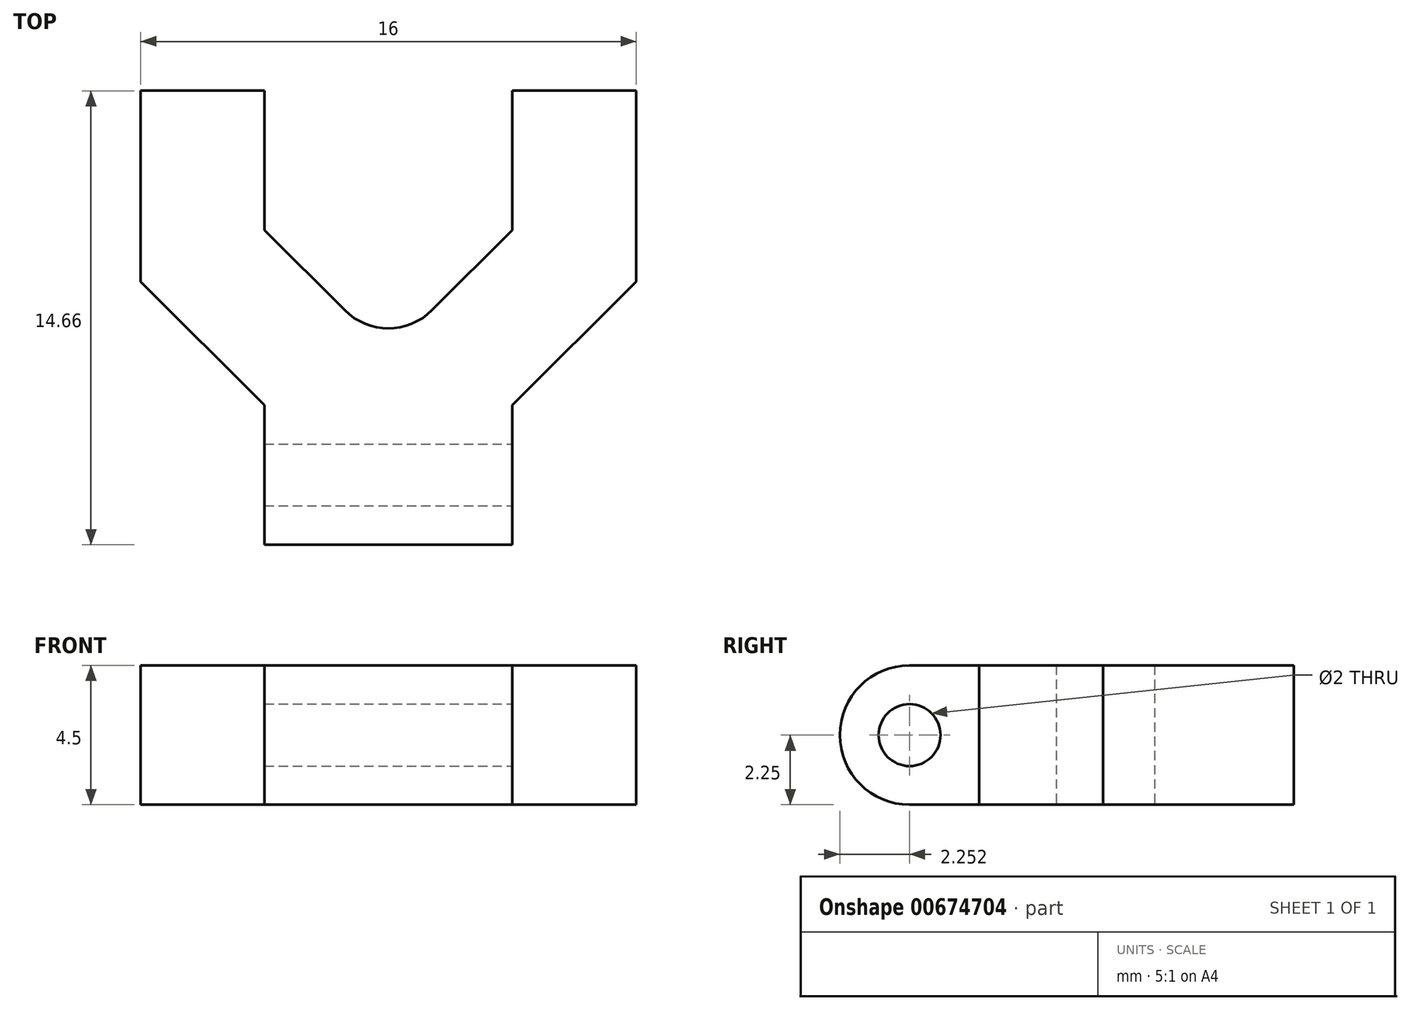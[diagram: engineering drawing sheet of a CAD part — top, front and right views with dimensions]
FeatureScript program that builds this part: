
annotation { "Feature Type Name" : "Feature", "Feature Type Description" : "" }
export const myFeature = defineFeature(function(context is Context, id is Id, definition is map)
    precondition{}
    {
        {
            var Q0;
            Q0=qCreatedBy(makeId("Top.planeOp"),FACE);
            var sketch = newSketch(context, id + "F0", { "sketchPlane" : qUnion([Q0])});
            skLineSegment(sketch, "E0", {"start": v(12.65, -1.09) * mm, "end": v(16.65, -1.09) * mm});
            skLineSegment(sketch, "E1", {"start": v(12.65, -1.09) * mm, "end": v(12.65, 5.07) * mm});
            skLineSegment(sketch, "E2", {"start": v(12.65, 5.07) * mm, "end": v(12.65, 20.92) * mm, "construction": true});
            skLineSegment(sketch, "E3", {"start": v(16.65, -1.09) * mm, "end": v(16.65, 19.23) * mm, "construction": true});
            skLineSegment(sketch, "E4", {"start": v(12.65, 5.07) * mm, "end": v(16.65, 9.07) * mm});
            skLineSegment(sketch, "E5", {"start": v(16.65, 9.07) * mm, "end": v(16.65, 13.57) * mm});
            skLineSegment(sketch, "E6", {"start": v(16.65, 13.57) * mm, "end": v(20.65, 13.57) * mm});
            skLineSegment(sketch, "E7", {"start": v(20.65, 13.57) * mm, "end": v(20.65, 7.41) * mm});
            skLineSegment(sketch, "E8", {"start": v(20.65, 7.41) * mm, "end": v(16.65, 3.41) * mm});
            skLineSegment(sketch, "E9", {"start": v(16.65, 3.41) * mm, "end": v(16.65, -1.09) * mm});
            skLineSegment(sketch, "E10", {"start": v(13.6, 11.57) * mm, "end": v(25.3, 11.57) * mm, "construction": true});
            skLineSegment(sketch, "E11", {"start": v(20.36, 0.91) * mm, "end": v(10.32, 0.91) * mm, "construction": true});
            skLineSegment(sketch, "E12.MirrorCS", {"start": v(11.7, 11.57) * mm, "end": v(0, 11.57) * mm, "construction": true});
            skLineSegment(sketch, "E13.MirrorCS", {"start": v(8.65, 9.07) * mm, "end": v(8.65, 13.57) * mm});
            skLineSegment(sketch, "E14.MirrorCS", {"start": v(12.65, -1.09) * mm, "end": v(8.65, -1.09) * mm});
            skLineSegment(sketch, "E15.MirrorCS", {"start": v(12.65, 5.07) * mm, "end": v(8.65, 9.07) * mm});
            skLineSegment(sketch, "E16.MirrorCS", {"start": v(8.65, 3.41) * mm, "end": v(8.65, -1.09) * mm});
            skLineSegment(sketch, "E17.MirrorCS", {"start": v(8.65, -1.09) * mm, "end": v(8.65, 19.23) * mm, "construction": true});
            skLineSegment(sketch, "E18.MirrorCS", {"start": v(4.65, 7.41) * mm, "end": v(8.65, 3.41) * mm});
            skLineSegment(sketch, "E19.MirrorCS", {"start": v(4.65, 13.57) * mm, "end": v(4.65, 7.41) * mm});
            skLineSegment(sketch, "E20.MirrorCS", {"start": v(8.65, 13.57) * mm, "end": v(4.65, 13.57) * mm});
            skLineSegment(sketch, "E21.MirrorCS", {"start": v(4.94, 0.91) * mm, "end": v(14.98, 0.91) * mm, "construction": true});
            skSolve(sketch);
        }
        {
            var Q0;
            Q0=makeQuery(id+"F0.imprint","IMPRINT",FACE,{"disambiguationData":[TD([[makeQuery(id+"F0.imprint","IMPRINT",EDGE,{"derivedFrom":sQuery(id+"F0.wireOp",EDGE,"E0")}),1.0]])]});
            var Q1;
            Q1=makeQuery(id+"F0.imprint","IMPRINT",FACE,{"disambiguationData":[TD([[makeQuery(id+"F0.imprint","IMPRINT",EDGE,{"derivedFrom":sQuery(id+"F0.wireOp",EDGE,"E13.MirrorCS")}),1.0]])]});
            extrude(context, id + "F1", {"entities" : qUnion([Q0, Q1]), "depth" : 4.5 * mm, "offsetDistance" : 25 * mm});
        }
        {
            var Q0;
            Q0=makeQuery(id+"F1.opExtrude","SWEPT_EDGE",EDGE,{"disambiguationData":[OSD([sQuery(id+"F0.wireOp",EDGE,"E4"),sQuery(id+"F0.wireOp",EDGE,"E15.MirrorCS"),sQuery(id+"F0.wireOp",EDGE,"E1")])]});
            fillet(context, id + "F2", {"entities" : qUnion([Q0]), "radius" : 2 * mm, "tangentPropagation" : true, "allowEdgeOverflow" : false});
        }
        {
            var Q0;
            Q0=makeQuery(id+"F1.opExtrude","SWEPT_FACE",FACE,{"disambiguationData":[OSD([sQuery(id+"F0.wireOp",EDGE,"E13.MirrorCS")])]});
            var sketch = newSketch(context, id + "F3", { "sketchPlane" : qUnion([Q0])});
            skLineSegment(sketch, "E22", {"start": v(13.57, 4.5) * mm, "end": v(9.07, 0) * mm, "construction": true});
            skLineSegment(sketch, "E23", {"start": v(13.57, 0) * mm, "end": v(9.07, 4.5) * mm, "construction": true});
            skSolve(sketch);
        }
        {
            var Q0;
            Q0=makeQuery(id+"F1.opExtrude","SWEPT_FACE",FACE,{"disambiguationData":[OSD([sQuery(id+"F0.wireOp",EDGE,"E9")])]});
            var sketch = newSketch(context, id + "F4", { "sketchPlane" : qUnion([Q0])});
            skLineSegment(sketch, "E24", {"start": v(3.41, 4.5) * mm, "end": v(-1.09, 0) * mm, "construction": true});
            skLineSegment(sketch, "E25", {"start": v(3.41, 0) * mm, "end": v(-1.09, 4.5) * mm, "construction": true});
            skCircle(sketch, "E26", {"center": v(1.16, 2.25) * mm, "radius": 1 * mm});
            skLineSegment(sketch, "E27", {"start": v(1.16, 2.25) * mm, "end": v(1.16, 4.5) * mm, "construction": true});
            skLineSegment(sketch, "E28", {"start": v(1.16, 2.25) * mm, "end": v(-1.09, 2.25) * mm, "construction": true});
            skLineSegment(sketch, "E29", {"start": v(1.16, 2.25) * mm, "end": v(1.16, 0) * mm, "construction": true});
            skArc(sketch, "E30", {"start": v(1.16, 4.5) * mm, "mid": v(-1.09, 2.25) * mm, "end": v(1.16, 0) * mm});
            skSolve(sketch);
        }
        {
            var Q0;
            Q0 = qSketchRegion(id + "F4", true);
            extrude(context, id + "F5", {"entities" : qUnion([Q0]), "operationType" : NewBodyOperationType.REMOVE, "oppositeDirection" : true, "depth" : 25 * mm, "offsetDistance" : 25 * mm});
        }
        {
            var Q0;
            Q0=makeQuery(id+"F1.opExtrude","CAP_EDGE",EDGE,{"disambiguationData":[OSD([sQuery(id+"F0.wireOp",EDGE,"E0"),sQuery(id+"F0.wireOp",EDGE,"E14.MirrorCS")])],"isStart":true});
            fillet(context, id + "F6", {"entities" : qUnion([Q0]), "radius" : 2.25 * mm, "tangentPropagation" : true, "allowEdgeOverflow" : false});
        }
        {
            var Q0;
            Q0=makeQuery(id+"F1.opExtrude","CAP_EDGE",EDGE,{"disambiguationData":[OSD([sQuery(id+"F0.wireOp",EDGE,"E0"),sQuery(id+"F0.wireOp",EDGE,"E14.MirrorCS")])],"isStart":false});
            fillet(context, id + "F7", {"entities" : qUnion([Q0]), "radius" : 2.25 * mm, "tangentPropagation" : true, "allowEdgeOverflow" : false});
        }
    });
